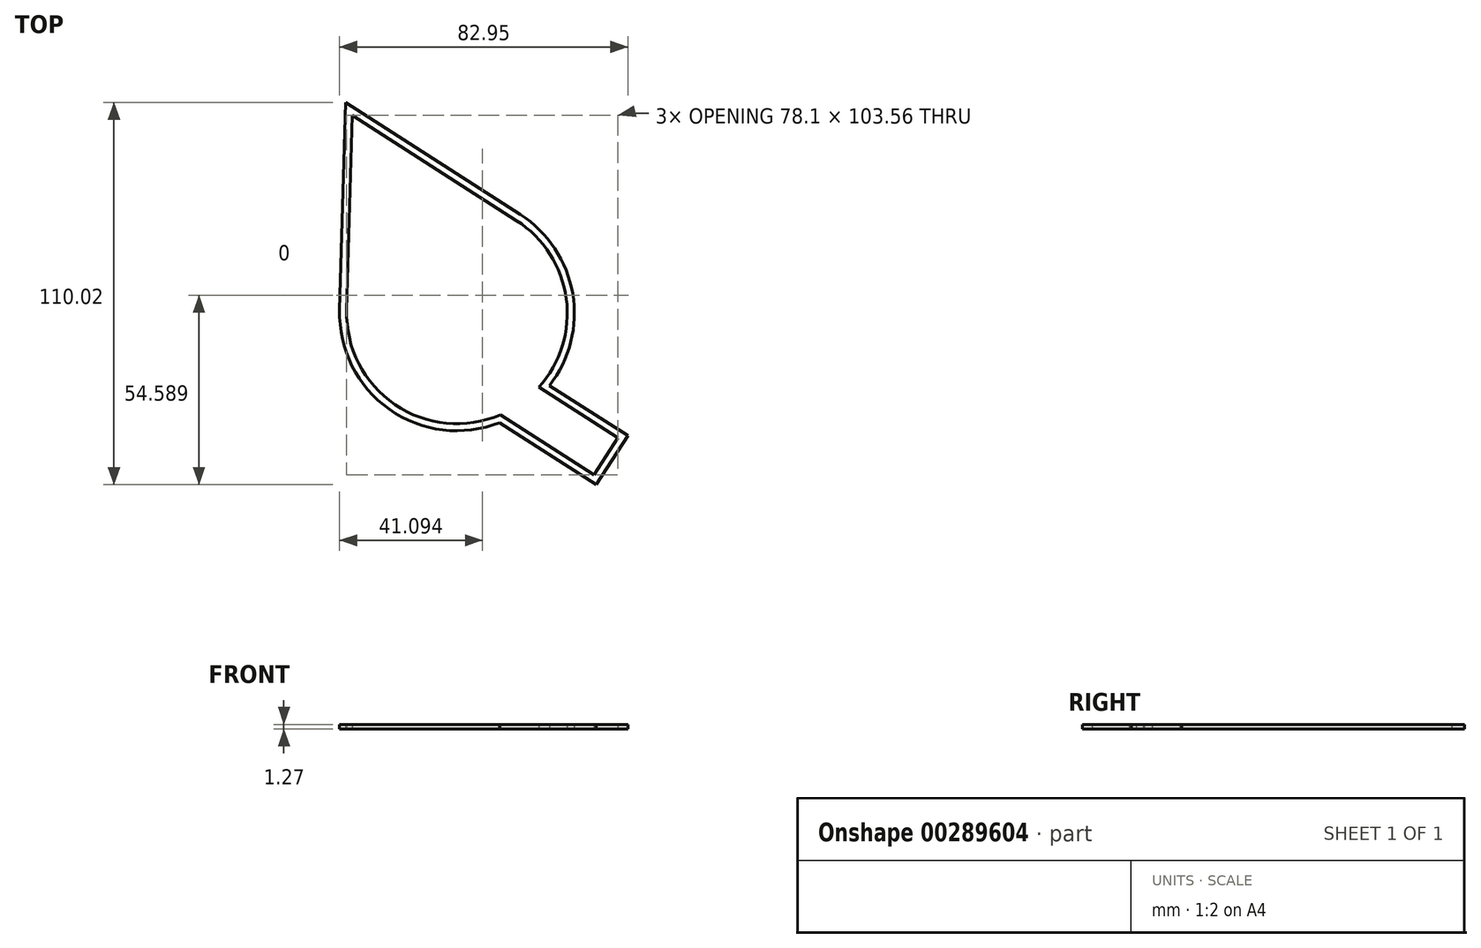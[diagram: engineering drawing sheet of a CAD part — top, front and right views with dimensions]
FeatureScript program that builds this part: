
annotation { "Feature Type Name" : "Feature", "Feature Type Description" : "" }
export const myFeature = defineFeature(function(context is Context, id is Id, definition is map)
    precondition{}
    {
        {
            var Q0;
            Q0=qCreatedBy(makeId("Top.planeOp"),FACE);
            var sketch = newSketch(context, id + "F0", { "sketchPlane" : qUnion([Q0])});
            skPoint(sketch, "E0", {"position": v(-27.54, 45.34) * mm});
            skLineSegment(sketch, "E1", {"start": v(-27.54, 45.34) * mm, "end": v(-29.17, -10.79) * mm});
            skLineSegment(sketch, "E2", {"start": v(-27.54, 45.34) * mm, "end": v(19.71, 15.02) * mm});
            skLineSegment(sketch, "E3", {"start": v(15.06, -40.9) * mm, "end": v(42.08, -58.22) * mm});
            skLineSegment(sketch, "E4", {"start": v(19.08, -37.75) * mm, "end": v(18.71, -37.13) * mm});
            skArc(sketch, "E5.trimOffspring", {"start": v(34.32, -11.7) * mm, "mid": v(30.43, 3.52) * mm, "end": v(19.71, 15.02) * mm});
            skLineSegment(sketch, "E6", {"start": v(6.68, -18.43) * mm, "end": v(-16.9, -12.98) * mm});
            skLineSegment(sketch, "E7", {"start": v(2.5, -11.46) * mm, "end": v(-17.12, -6.93) * mm});
            skLineSegment(sketch, "E8", {"start": v(-1.16, -5.39) * mm, "end": v(-17.3, -1.93) * mm});
            skLineSegment(sketch, "E9", {"start": v(-5, 1) * mm, "end": v(-17.5, 3.35) * mm});
            skLineSegment(sketch, "E10", {"start": v(-8.82, 7.37) * mm, "end": v(-17.7, 9.11) * mm});
            skLineSegment(sketch, "E11", {"start": v(18.13, -37.48) * mm, "end": v(19.65, -36.57) * mm});
            skLineSegment(sketch, "E12", {"start": v(19.65, -36.57) * mm, "end": v(-13.24, 18.19) * mm});
            skLineSegment(sketch, "E13", {"start": v(18.13, -37.48) * mm, "end": v(-14.81, 17.34) * mm});
            skLineSegment(sketch, "E14.0", {"start": v(3.14, -12.92) * mm, "end": v(-17.4, -8.17) * mm});
            skLineSegment(sketch, "E15.0", {"start": v(-0.5, -6.83) * mm, "end": v(-17.57, -3.17) * mm});
            skLineSegment(sketch, "E16.0", {"start": v(-8.16, 5.95) * mm, "end": v(-17.95, 7.86) * mm});
            skLineSegment(sketch, "E17", {"start": v(-17.19, -14.22) * mm, "end": v(-16.9, -12.98) * mm});
            skLineSegment(sketch, "E18", {"start": v(-17.4, -8.17) * mm, "end": v(-17.12, -6.93) * mm});
            skLineSegment(sketch, "E19", {"start": v(-17.57, -3.17) * mm, "end": v(-17.3, -1.93) * mm});
            skLineSegment(sketch, "E20", {"start": v(-17.73, 2.1) * mm, "end": v(-17.5, 3.35) * mm});
            skLineSegment(sketch, "E21", {"start": v(-17.95, 7.86) * mm, "end": v(-17.7, 9.11) * mm});
            skLineSegment(sketch, "E22", {"start": v(-17.19, -14.22) * mm, "end": v(7.59, -19.94) * mm});
            skLineSegment(sketch, "E23", {"start": v(3.14, -12.92) * mm, "end": v(3.4, -12.98) * mm});
            skLineSegment(sketch, "E24", {"start": v(-0.5, -6.83) * mm, "end": v(-0.26, -6.88) * mm});
            skLineSegment(sketch, "E25", {"start": v(-17.73, 2.1) * mm, "end": v(-4.12, -0.46) * mm});
            skLineSegment(sketch, "E26", {"start": v(-8.16, 5.95) * mm, "end": v(-7.94, 5.9) * mm});
            skLineSegment(sketch, "E27", {"start": v(-13.24, 18.19) * mm, "end": v(-14.81, 17.34) * mm});
            skArc(sketch, "E28.trimOffspring", {"start": v(-29.17, -10.79) * mm, "mid": v(-15.3, -37.95) * mm, "end": v(15.06, -40.9) * mm});
            skLineSegment(sketch, "E29", {"start": v(17.24, -36.01) * mm, "end": v(-17.86, -36.01) * mm});
            skLineSegment(sketch, "E30", {"start": v(15.88, -33.75) * mm, "end": v(-20.28, -33.75) * mm});
            skLineSegment(sketch, "E31", {"start": v(12.65, -28.37) * mm, "end": v(-24.46, -28.37) * mm});
            skLineSegment(sketch, "E32", {"start": v(11.05, -25.7) * mm, "end": v(-25.93, -25.7) * mm});
            skLineSegment(sketch, "E33", {"start": v(13.13, -25.7) * mm, "end": v(31.06, -25.7) * mm});
            skLineSegment(sketch, "E34", {"start": v(14.73, -28.37) * mm, "end": v(29.6, -28.37) * mm});
            skLineSegment(sketch, "E35", {"start": v(9.1, -22.44) * mm, "end": v(-27.31, -22.44) * mm});
            skLineSegment(sketch, "E36", {"start": v(11.16, -22.44) * mm, "end": v(32.45, -22.44) * mm});
            skLineSegment(sketch, "E37", {"start": v(9.44, -18.43) * mm, "end": v(33.6, -18.43) * mm});
            skLineSegment(sketch, "E38", {"start": v(0.95, -18.4) * mm, "end": v(-28.47, -18.4) * mm});
            skLineSegment(sketch, "E39", {"start": v(20.32, -0.04) * mm, "end": v(19.29, 0.7) * mm});
            skLineSegment(sketch, "E40", {"start": v(-7.15, 8.04) * mm, "end": v(-2.29, 16.24) * mm});
            skLineSegment(sketch, "E41", {"start": v(-1.25, 15.5) * mm, "end": v(-6.4, 6.8) * mm});
            skLineSegment(sketch, "E42", {"start": v(-3.33, 1.68) * mm, "end": v(3.03, 12.41) * mm});
            skLineSegment(sketch, "E43", {"start": v(0.51, -4.72) * mm, "end": v(8.38, 8.56) * mm});
            skLineSegment(sketch, "E44", {"start": v(4.17, -10.8) * mm, "end": v(13.47, 4.9) * mm});
            skLineSegment(sketch, "E45", {"start": v(8.35, -17.75) * mm, "end": v(19.29, 0.7) * mm});
            skLineSegment(sketch, "E46.trimOffspring", {"start": v(14.5, 4.15) * mm, "end": v(13.47, 4.9) * mm});
            skLineSegment(sketch, "E47.trimOffspring", {"start": v(9.42, 7.81) * mm, "end": v(8.38, 8.56) * mm});
            skLineSegment(sketch, "E48.trimOffspring", {"start": v(4.06, 11.67) * mm, "end": v(3.03, 12.41) * mm});
            skLineSegment(sketch, "E49", {"start": v(4.06, 11.67) * mm, "end": v(-2.59, 0.45) * mm});
            skLineSegment(sketch, "E50", {"start": v(9.42, 7.81) * mm, "end": v(1.26, -5.95) * mm});
            skLineSegment(sketch, "E51", {"start": v(14.5, 4.15) * mm, "end": v(4.91, -12.04) * mm});
            skLineSegment(sketch, "E52", {"start": v(20.32, -0.04) * mm, "end": v(9.1, -19) * mm});
            skLineSegment(sketch, "E53", {"start": v(9.44, -18.43) * mm, "end": v(9.42, -18.43) * mm});
            skLineSegment(sketch, "E54.trimOffspring", {"start": v(-1.25, 15.5) * mm, "end": v(-2.29, 16.24) * mm});
            skLineSegment(sketch, "E55", {"start": v(48.94, -47.53) * mm, "end": v(26.18, -32.93) * mm});
            skLineSegment(sketch, "E56", {"start": v(48.94, -47.53) * mm, "end": v(42.08, -58.22) * mm});
            skArc(sketch, "E57.trimOffspring", {"start": v(26.18, -32.93) * mm, "mid": v(32.21, -23.07) * mm, "end": v(34.32, -11.7) * mm});
            skPoint(sketch, "E58.start.orphan", {"position": v(17.96, -33.75) * mm});
            skPoint(sketch, "E59.start.orphan", {"position": v(19.32, -36.01) * mm});
            skLineSegment(sketch, "E60.0", {"start": v(-29.47, 49) * mm, "end": v(20.81, 16.73) * mm});
            skArc(sketch, "E60.1", {"start": v(36.35, -11.7) * mm, "mid": v(32.21, 4.5) * mm, "end": v(20.81, 16.73) * mm});
            skLineSegment(sketch, "E60.2", {"start": v(-29.47, 49) * mm, "end": v(-31.2, -10.73) * mm});
            skArc(sketch, "E60.3", {"start": v(29.22, -32.47) * mm, "mid": v(34.52, -22.68) * mm, "end": v(36.35, -11.7) * mm});
            skArc(sketch, "E60.4", {"start": v(-31.2, -10.73) * mm, "mid": v(-16.89, -39.32) * mm, "end": v(14.86, -43.17) * mm});
            skLineSegment(sketch, "E60.5", {"start": v(14.86, -43.17) * mm, "end": v(42.7, -61.03) * mm});
            skLineSegment(sketch, "E60.6", {"start": v(51.74, -46.92) * mm, "end": v(42.7, -61.03) * mm});
            skLineSegment(sketch, "E60.7", {"start": v(51.74, -46.92) * mm, "end": v(29.22, -32.47) * mm});
            skSolve(sketch);
        }
        {
            var Q0;
            {var subQ11=sQuery(id+"F0.wireOp",EDGE,"E1");Q0=makeQuery(id+"F0.imprint","IMPRINT",FACE,{"disambiguationData":[TD([[makeQuery(id+"F0.imprint","IMPRINT",EDGE,{"derivedFrom":subQ11}),-1.0]])]});}
            extrude(context, id + "F1", {"entities" : qUnion([Q0]), "depth" : 1.27 * mm});
        }
    });
